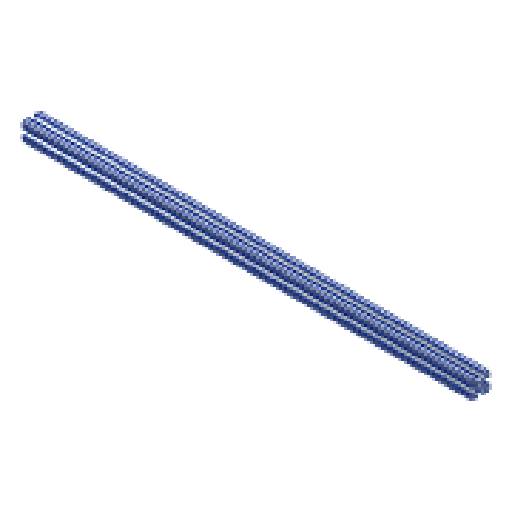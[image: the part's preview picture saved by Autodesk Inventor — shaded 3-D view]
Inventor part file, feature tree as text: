
AUTODESK INVENTOR PART (.ipt)
format: ipt  version: 2025 (Build 290162000, 162)  size: 216,576 bytes
history: native  units: in
note: dims shown in document units (in); Inventor stores cm internally (conversion verified against a paired STEP export)
features: extrude x1, sketch x1
ambient origin geometry x8: Origin, YZ Plane, XZ Plane, XY Plane, X Axis, Y Axis, Z Axis, Center Point
bodies: Solid1 (feature_tree)
feature tree (2):
  extrude  "Extrusion1"  [1 undecoded]
  sketch  "Sketch1"  dims[d0=24.0in d1=0.0in]
note: 1 required parameter value undecoded (feature->parameter linkage not recoverable at this tier; creation-order binding heuristic only, values carry confidence <= 0.55)
